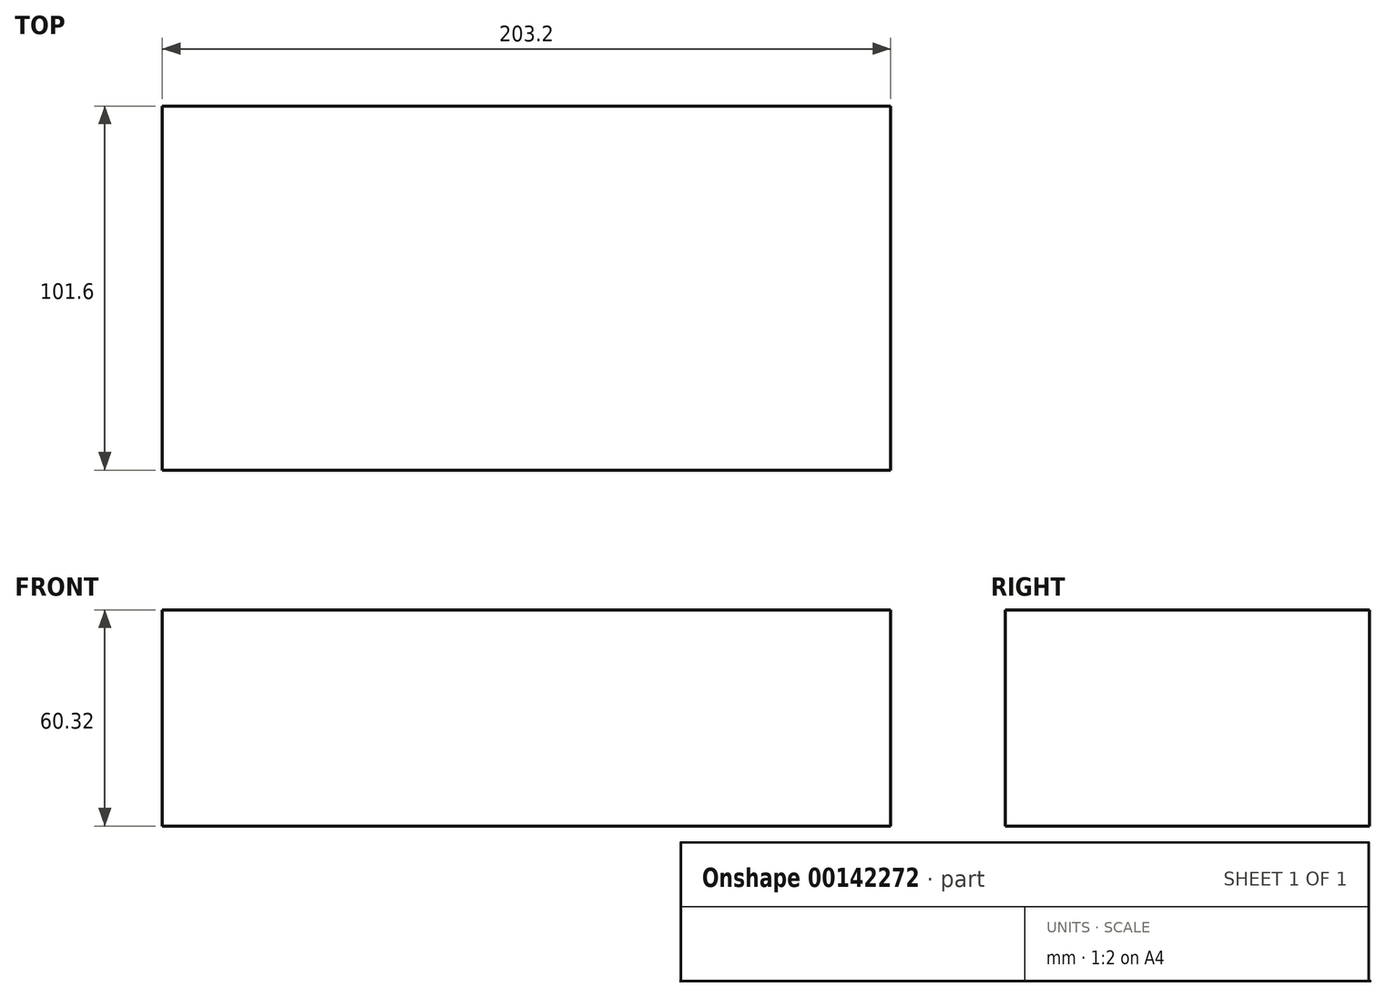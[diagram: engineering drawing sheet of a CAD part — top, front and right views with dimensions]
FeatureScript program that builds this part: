
annotation { "Feature Type Name" : "Feature", "Feature Type Description" : "" }
export const myFeature = defineFeature(function(context is Context, id is Id, definition is map)
    precondition{}
    {
        {
            var Q0;
            Q0=qCreatedBy(makeId("Top.planeOp"),FACE);
            var sketch = newSketch(context, id + "F0", { "sketchPlane" : qUnion([Q0])});
            skLineSegment(sketch, "E0.bottom", {"start": v(0, 0) * mm, "end": v(203.2, 0) * mm});
            skLineSegment(sketch, "E0.top", {"start": v(0, -101.6) * mm, "end": v(203.2, -101.6) * mm});
            skLineSegment(sketch, "E0.left", {"start": v(0, 0) * mm, "end": v(0, -101.6) * mm});
            skLineSegment(sketch, "E0.right", {"start": v(203.2, 0) * mm, "end": v(203.2, -101.6) * mm});
            skSolve(sketch);
        }
        {
            var Q0;
            Q0 = qSketchRegion(id + "F0", true);
            extrude(context, id + "F1", {"entities" : qUnion([Q0]), "depth" : 60.32 * mm});
        }
    });
